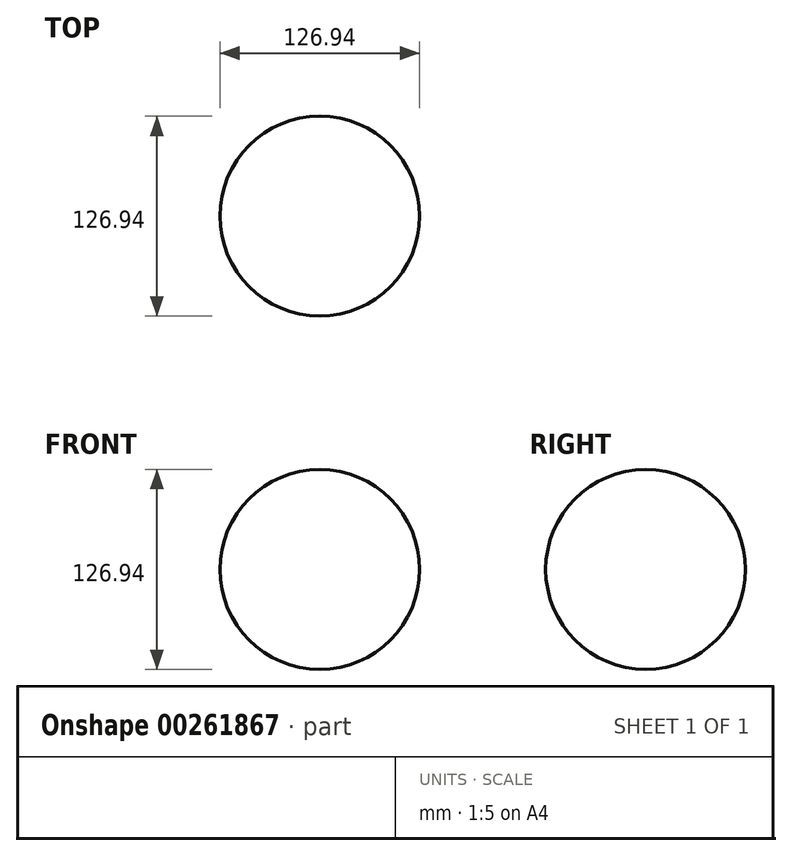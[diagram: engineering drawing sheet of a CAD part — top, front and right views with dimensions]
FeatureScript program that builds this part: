
annotation { "Feature Type Name" : "Feature", "Feature Type Description" : "" }
export const myFeature = defineFeature(function(context is Context, id is Id, definition is map)
    precondition{}
    {
        {
            var Q0;
            Q0=qCreatedBy(makeId("Front.planeOp"),FACE);
            var sketch = newSketch(context, id + "F0", { "sketchPlane" : qUnion([Q0])});
            skLineSegment(sketch, "E0", {"start": v(0, -113.4) * mm, "end": v(0, 103.56) * mm, "construction": true});
            skArc(sketch, "E1", {"start": v(0, 63.47) * mm, "mid": v(-63.47, 0) * mm, "end": v(0, -63.47) * mm});
            skSolve(sketch);
        }
        {
            var Q0;
            Q0=sQuery(id+"F0.wireOp",EDGE,"E1");
            var Q1;
            Q1=sQuery(id+"F0.wireOp",EDGE,"E0");
            revolve(context, id + "F1", {"bodyType" : ToolBodyType.SURFACE, "surfaceEntities" : qUnion([Q0]), "axis" : qUnion([Q1]), "revolveType" : RevolveType.FULL});
        }
    });
